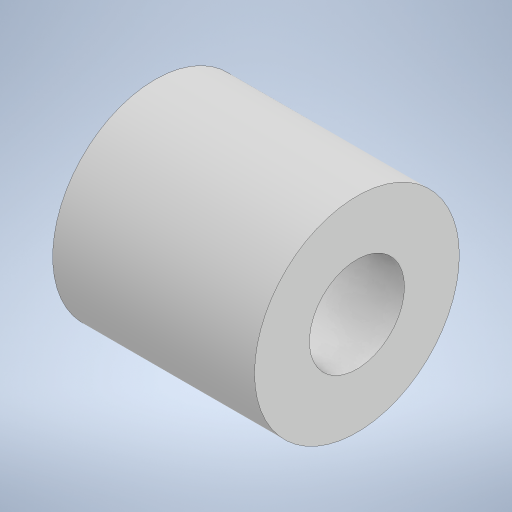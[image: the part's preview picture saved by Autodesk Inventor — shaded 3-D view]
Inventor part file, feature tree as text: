
AUTODESK INVENTOR PART (.ipt)
format: ipt  version: 2023 (Build 270158000, 158)  size: 216,576 bytes
history: native  units: mm
features: extrude x2, sketch x2, other x1
ambient origin geometry x8: Origin, YZ Plane, XZ Plane, XY Plane, X Axis, Y Axis, Z Axis, Center Point
bodies: Body1 (feature_tree)
feature tree (5):
  other  "Bryła1"
  extrude  "Wyciągnięcie proste1"  Depth=14.0mm
  extrude  "Wyciągnięcie proste2"  Depth=2.0mm
  sketch  "Szkic1"
  sketch  "Szkic2"
